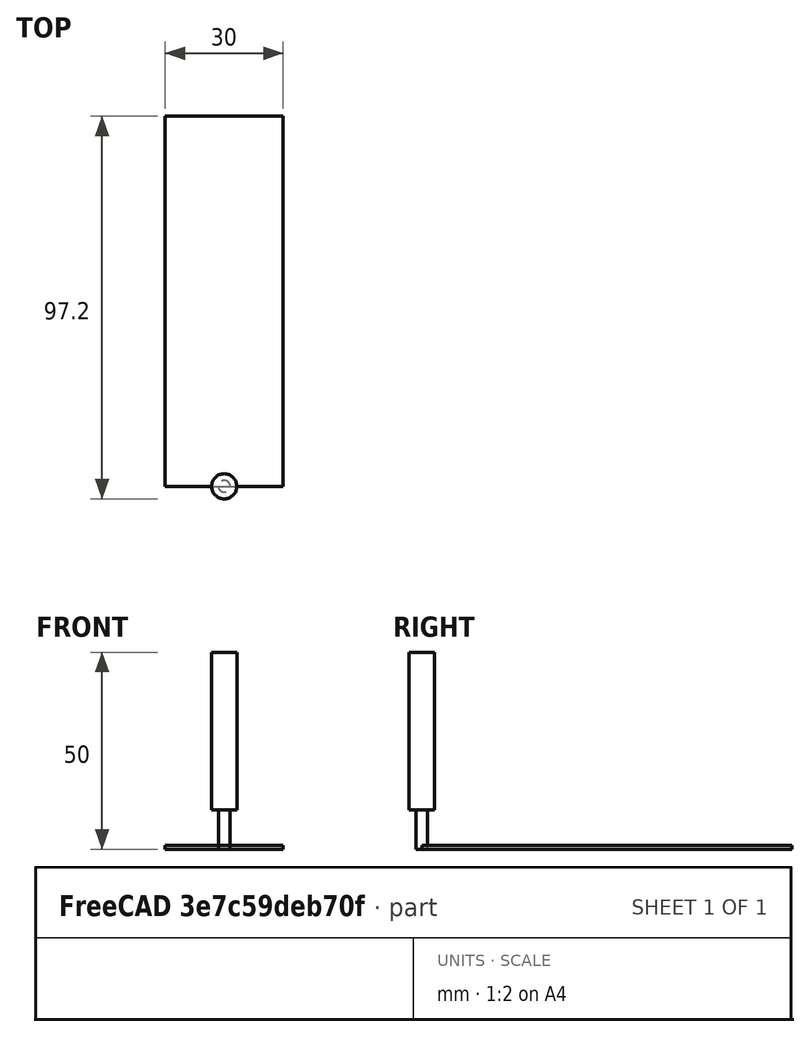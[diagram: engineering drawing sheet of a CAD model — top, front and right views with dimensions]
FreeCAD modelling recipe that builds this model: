
FCSTD DOCUMENT  (FreeCAD 0.20RUnknown)
Label: MySinSpline
License: All rights reserved
LicenseURL: http://en.wikipedia.org/wiki/All_rights_reserved
objects: App::DocumentObjectGroup×3, Path::FeaturePython×3, Part::Part2DObjectPython×2, Part::FeaturePython×2, App::FeaturePython×1, Part::Offset2D×1
note: 5 computed .brp shape members not serialized (recipe doc carries the construction recipe); baked Part::Feature solids carry a one-line shape summary decoded from their .brp

FEATURE [Part::Part2DObjectPython] BSpline  # Draft 2D object (typed FeaturePython)
  Area = 0
  Closed = false
  MakeFace = true
  Parameterization = 1
  Points = (189) [(0,0,0),(1.4975,0.5,0),(2.98004,1,0),(4.4328,1.5,0),(5.84128,2,0),(7.19138,2.5,0),(8.46964,3,0),(9.66327,3.5,0),(10.7603,4,0),(11.7499,4.5,0),+179 more]
FEATURE [App::FeaturePython] SetupSheet  # Path/CAM operation (typed FeaturePython)
  ClearanceHeightExpression = OpStockZMax+SetupSheet.ClearanceHeightOffset
  ClearanceHeightOffset = 5
  CoolantMode = 0
  CoolantModes = None | Flood | Mist
  FinalDepthExpression = OpFinalDepth
  HorizRapid = 0
  SafeHeightExpression = OpStockZMax+SetupSheet.SafeHeightOffset
  SafeHeightOffset = 3
  StartDepthExpression = OpStartDepth
  StepDownExpression = OpToolDiameter
  VertRapid = 0
FEATURE [Part::Part2DObjectPython] Clone2D  label="Model-BSpline"  # Draft 2D object (typed FeaturePython)
  Fuse = false
  Objects = -> [BSpline]
  PathResource = Model
  Scale = (1,1,1)
FEATURE [App::DocumentObjectGroup] Model
  Group = -> [Clone2D]
FEATURE [Part::FeaturePython] Stock001  # WARN: FeaturePython — macro-defined, semantics opaque (R4)
  Height = 1
  Length = 30
  Placement = pos=(-14.9994,0,0) rot=(0,0,1;0rad)
  StockType = CreateBox
  Width = 94
FEATURE [Part::FeaturePython] ToolBit001  label="3mm_Endmill"  # Path/CAM toolbit (typed FeaturePython)
  BitPropertyNames = Chipload | CuttingEdgeHeight | Diameter | Flutes | Length | Material | ShankDiameter | SpindleDirection
  BitShape = <path>
  Chipload = 0
  CuttingEdgeHeight = 10
  Diameter = 3
  File = <userpath>/Documents/Sherline/FreeCAD/Bit/3mm_Endmill.fctb
  Flutes = 0
  Length = 50
  Material = 0
  ShankDiameter = 6.4
  ShapeName = endmill
  SpindleDirection = 0
FEATURE [Path::FeaturePython] _mm_Endmill  label="3mm_Endmill001"  # Path/CAM operation (typed FeaturePython)
  HorizFeed = 8.33333
  HorizRapid = 0
  SpindleDir = 0
  SpindleSpeed = 10000
  Tool = -> ToolBit001
  ToolNumber = 2
  VertFeed = 1.66667
  VertRapid = 0
  expr: HorizRapid = SetupSheet.HorizRapid
  expr: VertRapid = SetupSheet.VertRapid
FEATURE [App::DocumentObjectGroup] Tools
  Group = -> [_mm_Endmill]
FEATURE [Path::FeaturePython] Engrave  # Path/CAM operation (typed FeaturePython)
  Active = true
  Base = -> [Clone2D]
  ClearanceHeight = 6
  CoolantMode = 0
  CycleTime = 00:01:28
  FinalDepth = -4
  OpFinalDepth = -2
  OpStartDepth = 0
  OpStockZMax = 1
  OpStockZMin = 0
  OpToolDiameter = 3
  SafeHeight = 4
  StartDepth = 0
  StartVertex = 0
  StepDown = 2
  ToolController = -> _mm_Endmill
  expr: ClearanceHeight = OpStockZMax + SetupSheet.ClearanceHeightOffset
  expr: FinalDepth = -4
  expr: SafeHeight = OpStockZMax + SetupSheet.SafeHeightOffset
  expr: StartDepth = OpStartDepth
  expr: StepDown = 2
FEATURE [App::DocumentObjectGroup] Operations
  Group = -> [Engrave]
FEATURE [Path::FeaturePython] Job  # Path/CAM operation (typed FeaturePython)
  CycleTime = 00:01:28
  Fixtures = G54
  GeometryTolerance = 0.01
  JobType = 0
  Model = -> Model
  Operations = -> Operations
  OrderOutputBy = 0
  PostProcessor = 2
  PostProcessorOutputFile = %D/%d-%j.ngc
  SetupSheet = -> SetupSheet
  SplitOutput = false
  Stock = -> Stock001
  Tools = -> Tools
FEATURE [Part::Offset2D] Offset2D
  Fill = false
  Intersection = false
  Join = 0
  Mode = 1
  SelfIntersection = false
  Source = -> BSpline
  Value = 1.5
note: 1 file-system path scrubbed to <path> (originals preserved in the JSON sidecar)
